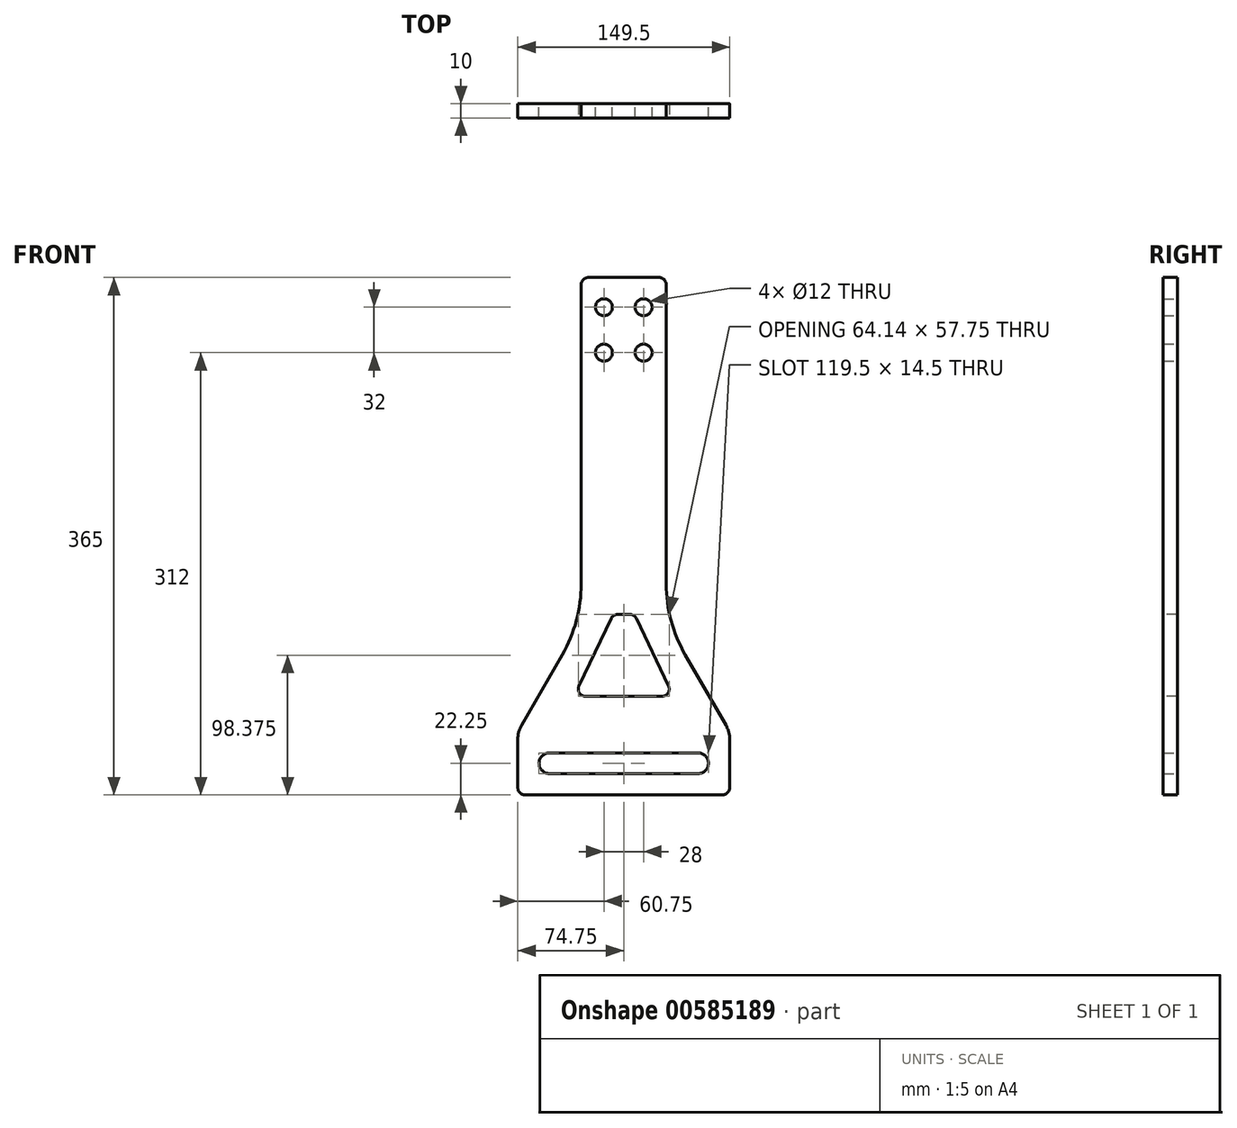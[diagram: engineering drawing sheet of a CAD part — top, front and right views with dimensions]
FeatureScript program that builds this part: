
annotation { "Feature Type Name" : "Feature", "Feature Type Description" : "" }
export const myFeature = defineFeature(function(context is Context, id is Id, definition is map)
    precondition{}
    {
        {
            var Q0;
            Q0=qCreatedBy(makeId("Front.planeOp"),FACE);
            var sketch = newSketch(context, id + "F0", { "sketchPlane" : qUnion([Q0])});
            skLineSegment(sketch, "E0.bottom", {"start": v(0, 0) * mm, "end": v(105, 0) * mm});
            skLineSegment(sketch, "E0.top", {"start": v(0, 14.5) * mm, "end": v(105, 14.5) * mm});
            skLineSegment(sketch, "E0.left", {"start": v(0, 0) * mm, "end": v(0, 14.5) * mm, "construction": true});
            skLineSegment(sketch, "E0.right", {"start": v(105, 0) * mm, "end": v(105, 14.5) * mm, "construction": true});
            skArc(sketch, "E1", {"start": v(0, 14.5) * mm, "mid": v(-7.25, 7.25) * mm, "end": v(0, 0) * mm});
            skArc(sketch, "E2", {"start": v(105, 0) * mm, "mid": v(112.25, 7.25) * mm, "end": v(105, 14.5) * mm});
            skLineSegment(sketch, "E3.bottom", {"start": v(-17.25, -15) * mm, "end": v(122.25, -15) * mm});
            skLineSegment(sketch, "E3.top", {"start": v(-17.25, 29.5) * mm, "end": v(97.5, 29.5) * mm});
            skLineSegment(sketch, "E3.left", {"start": v(-22.25, -10) * mm, "end": v(-22.25, 24.14) * mm});
            skLineSegment(sketch, "E3.right", {"start": v(127.25, -10) * mm, "end": v(127.25, 24.14) * mm});
            skPoint(sketch, "E4.visualSharp", {"position": v(-22.25, 29.5) * mm});
            skArc(sketch, "E4.filletArc", {"start": v(-17.25, 29.5) * mm, "mid": v(-20.79, 28.04) * mm, "end": v(-22.25, 24.5) * mm, "construction": true});
            skPoint(sketch, "E5.visualSharp", {"position": v(-22.25, -15) * mm});
            skArc(sketch, "E5.filletArc", {"start": v(-22.25, -10) * mm, "mid": v(-20.79, -13.54) * mm, "end": v(-17.25, -15) * mm});
            skPoint(sketch, "E6.visualSharp", {"position": v(127.25, -15) * mm});
            skArc(sketch, "E6.filletArc", {"start": v(122.25, -15) * mm, "mid": v(125.79, -13.54) * mm, "end": v(127.25, -10) * mm});
            skPoint(sketch, "E7.visualSharp", {"position": v(127.25, 29.5) * mm});
            skArc(sketch, "E7.filletArc", {"start": v(127.25, 24.5) * mm, "mid": v(125.79, 28.04) * mm, "end": v(122.25, 29.5) * mm, "construction": true});
            skLineSegment(sketch, "E8.top", {"start": v(27.5, 350) * mm, "end": v(77.5, 350) * mm});
            skLineSegment(sketch, "E8.left", {"start": v(22.5, 133.8) * mm, "end": v(22.5, 345) * mm});
            skLineSegment(sketch, "E8.right", {"start": v(82.5, 133.8) * mm, "end": v(82.5, 345) * mm});
            skPoint(sketch, "E9", {"position": v(52.5, 350) * mm});
            skLineSegment(sketch, "E10.trimOffspring", {"start": v(97.5, 29.5) * mm, "end": v(122.25, 29.5) * mm, "construction": true});
            skPoint(sketch, "E11.visualSharp", {"position": v(22.5, 29.5) * mm});
            skPoint(sketch, "E12.visualSharp", {"position": v(82.5, 29.5) * mm});
            skPoint(sketch, "E13.visualSharp", {"position": v(22.5, 350) * mm});
            skArc(sketch, "E13.filletArc", {"start": v(27.5, 350) * mm, "mid": v(23.96, 348.54) * mm, "end": v(22.5, 345) * mm});
            skPoint(sketch, "E14.visualSharp", {"position": v(82.5, 350) * mm});
            skArc(sketch, "E14.filletArc", {"start": v(82.5, 345) * mm, "mid": v(81.04, 348.54) * mm, "end": v(77.5, 350) * mm});
            skLineSegment(sketch, "E15", {"start": v(-19.57, 34.14) * mm, "end": v(9.1, 83.8) * mm});
            skLineSegment(sketch, "E16", {"start": v(22.5, 107) * mm, "end": v(82.5, 107) * mm, "construction": true});
            skLineSegment(sketch, "E17", {"start": v(95.9, 83.8) * mm, "end": v(124.57, 34.14) * mm});
            skPoint(sketch, "E18.visualSharp", {"position": v(22.5, 107) * mm});
            skArc(sketch, "E18.filletArc", {"start": v(9.1, 83.8) * mm, "mid": v(19.1, 107.92) * mm, "end": v(22.5, 133.8) * mm});
            skPoint(sketch, "E19.visualSharp", {"position": v(82.5, 107) * mm});
            skArc(sketch, "E19.filletArc", {"start": v(82.5, 133.8) * mm, "mid": v(85.9, 107.92) * mm, "end": v(95.9, 83.8) * mm});
            skArc(sketch, "E20.filletArc", {"start": v(-19.57, 34.14) * mm, "mid": v(-21.57, 29.32) * mm, "end": v(-22.25, 24.14) * mm});
            skArc(sketch, "E21.filletArc", {"start": v(127.25, 24.14) * mm, "mid": v(126.57, 29.32) * mm, "end": v(124.57, 34.14) * mm});
            skCircle(sketch, "E22", {"center": v(38.5, 329) * mm, "radius": 6 * mm});
            skCircle(sketch, "E23", {"center": v(66.5, 329) * mm, "radius": 6 * mm});
            skCircle(sketch, "E24", {"center": v(38.5, 297) * mm, "radius": 6 * mm});
            skCircle(sketch, "E25", {"center": v(66.5, 297) * mm, "radius": 6 * mm});
            skSolve(sketch);
        }
        {
            var Q0;
            Q0 = qSketchRegion(id + "F0", true);
            extrude(context, id + "F1", {"entities" : qUnion([Q0]), "depth" : 10 * mm, "offsetDistance" : 25 * mm});
        }
        {
            var Q0;
            Q0=makeQuery(id+"F1.opExtrude","CAP_FACE",FACE,{"disambiguationData":[OSD([sQuery(id+"F0.wireOp",EDGE,"E0.bottom"),sQuery(id+"F0.wireOp",EDGE,"E0.top"),sQuery(id+"F0.wireOp",EDGE,"E1"),sQuery(id+"F0.wireOp",EDGE,"E2"),sQuery(id+"F0.wireOp",EDGE,"E3.bottom"),sQuery(id+"F0.wireOp",EDGE,"E3.left"),sQuery(id+"F0.wireOp",EDGE,"E3.right"),sQuery(id+"F0.wireOp",EDGE,"E5.filletArc"),sQuery(id+"F0.wireOp",EDGE,"E6.filletArc"),sQuery(id+"F0.wireOp",EDGE,"E8.top"),sQuery(id+"F0.wireOp",EDGE,"E8.left"),sQuery(id+"F0.wireOp",EDGE,"E8.right"),sQuery(id+"F0.wireOp",EDGE,"E13.filletArc"),sQuery(id+"F0.wireOp",EDGE,"E14.filletArc"),sQuery(id+"F0.wireOp",EDGE,"IPP8U5lv-fXUz-ytd3-fDjt-NUQY1XdNgHQK"),sQuery(id+"F0.wireOp",EDGE,"E15"),sQuery(id+"F0.wireOp",EDGE,"E17"),sQuery(id+"F0.wireOp",EDGE,"E18.filletArc"),sQuery(id+"F0.wireOp",EDGE,"E19.filletArc"),sQuery(id+"F0.wireOp",EDGE,"E20.filletArc"),sQuery(id+"F0.wireOp",EDGE,"E21.filletArc")])],"isStart":false});
            var sketch = newSketch(context, id + "F2", { "sketchPlane" : qUnion([Q0])});
            skLineSegment(sketch, "E26", {"start": v(43.64, 109.4) * mm, "end": v(20.9, 61.65) * mm});
            skLineSegment(sketch, "E27", {"start": v(25.42, 54.5) * mm, "end": v(79.58, 54.5) * mm});
            skLineSegment(sketch, "E28", {"start": v(84.1, 61.65) * mm, "end": v(61.36, 109.4) * mm});
            skLineSegment(sketch, "E29", {"start": v(56.84, 112.25) * mm, "end": v(48.16, 112.25) * mm});
            skPoint(sketch, "E30", {"position": v(52.5, 112.25) * mm});
            skPoint(sketch, "E31", {"position": v(52.5, 182.25) * mm});
            skPoint(sketch, "E32", {"position": v(52.5, 54.5) * mm});
            skPoint(sketch, "E33.visualSharp", {"position": v(45, 112.25) * mm});
            skArc(sketch, "E33.filletArc", {"start": v(48.16, 112.25) * mm, "mid": v(45.49, 111.48) * mm, "end": v(43.64, 109.4) * mm});
            skPoint(sketch, "E34.visualSharp", {"position": v(60, 112.25) * mm});
            skArc(sketch, "E34.filletArc", {"start": v(61.36, 109.4) * mm, "mid": v(59.51, 111.48) * mm, "end": v(56.84, 112.25) * mm});
            skPoint(sketch, "E35.visualSharp", {"position": v(87.5, 54.5) * mm});
            skArc(sketch, "E35.filletArc", {"start": v(79.58, 54.5) * mm, "mid": v(83.8, 56.83) * mm, "end": v(84.1, 61.65) * mm});
            skPoint(sketch, "E36.visualSharp", {"position": v(17.5, 54.5) * mm});
            skArc(sketch, "E36.filletArc", {"start": v(20.9, 61.65) * mm, "mid": v(21.2, 56.83) * mm, "end": v(25.42, 54.5) * mm});
            skSolve(sketch);
        }
        {
            var Q0;
            Q0 = qSketchRegion(id + "F2", true);
            extrude(context, id + "F3", {"entities" : qUnion([Q0]), "operationType" : NewBodyOperationType.REMOVE, "oppositeDirection" : true, "depth" : 25 * mm, "offsetDistance" : 25 * mm});
        }
    });
